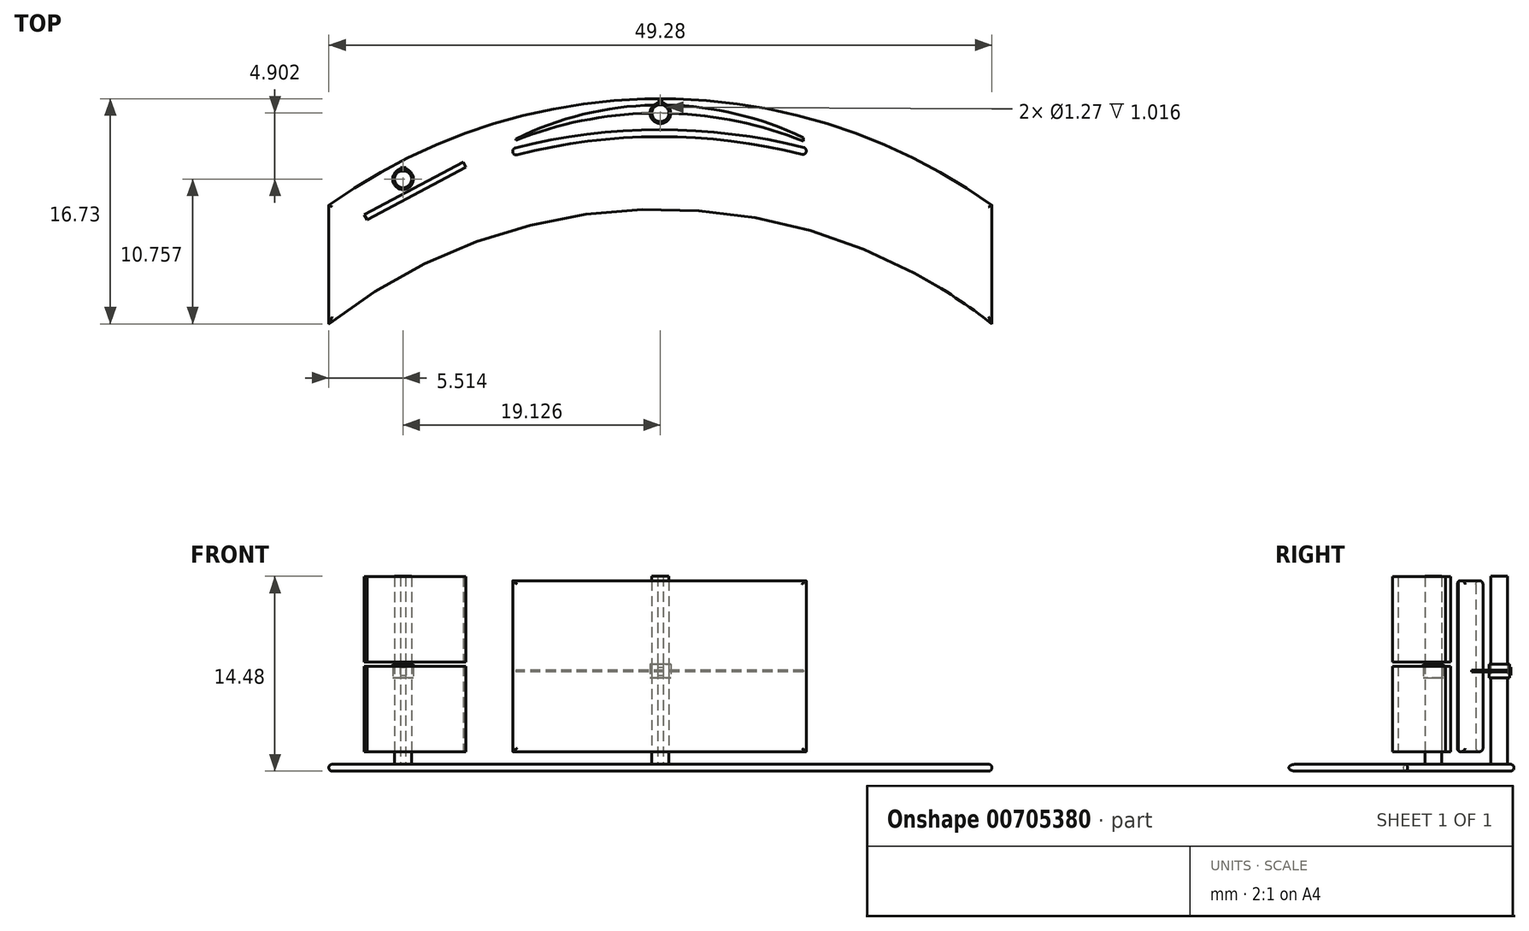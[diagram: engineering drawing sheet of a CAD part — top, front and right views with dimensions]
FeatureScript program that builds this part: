
annotation { "Feature Type Name" : "Feature", "Feature Type Description" : "" }
export const myFeature = defineFeature(function(context is Context, id is Id, definition is map)
    precondition{}
    {
        {
            var Q0;
            Q0=qCreatedBy(makeId("Top.planeOp"),FACE);
            var sketch = newSketch(context, id + "F0", { "sketchPlane" : qUnion([Q0])});
            skArc(sketch, "E0", {"start": v(24.64, 0) * mm, "mid": v(0, 7.91) * mm, "end": v(-24.64, 0) * mm});
            skLineSegment(sketch, "E1", {"start": v(-24.64, 0) * mm, "end": v(-24.64, -8.82) * mm});
            skLineSegment(sketch, "E2", {"start": v(24.64, -8.82) * mm, "end": v(24.64, 0) * mm});
            skArc(sketch, "E3", {"start": v(24.64, -8.82) * mm, "mid": v(0, -0.3) * mm, "end": v(-24.64, -8.82) * mm});
            skCircle(sketch, "E4", {"center": v(0, 6.84) * mm, "radius": 0.64 * mm});
            skCircle(sketch, "E5", {"center": v(-19.12, 1.94) * mm, "radius": 0.64 * mm});
            skCircle(sketch, "E6", {"center": v(18.32, 1.94) * mm, "radius": 0.64 * mm});
            skArc(sketch, "E7", {"start": v(10.63, 5) * mm, "mid": v(-0.07, 7.44) * mm, "end": v(-10.75, 4.93) * mm});
            skLineSegment(sketch, "E8", {"start": v(-10.75, 4.93) * mm, "end": v(-10.75, 4.83) * mm});
            skLineSegment(sketch, "E9", {"start": v(10.63, 5) * mm, "end": v(10.63, 4.75) * mm});
            skArc(sketch, "E10", {"start": v(10.63, 4.75) * mm, "mid": v(-0.06, 6.84) * mm, "end": v(-10.75, 4.83) * mm});
            skCircle(sketch, "E11", {"center": v(0, 6.84) * mm, "radius": 0.77 * mm});
            skLineSegment(sketch, "E12.bottom", {"start": v(-0.21, 7.58) * mm, "end": v(0.2, 7.58) * mm});
            skLineSegment(sketch, "E12.top", {"start": v(-0.21, 7.7) * mm, "end": v(0.2, 7.7) * mm});
            skLineSegment(sketch, "E12.left", {"start": v(-0.21, 7.58) * mm, "end": v(-0.21, 7.7) * mm});
            skLineSegment(sketch, "E12.right", {"start": v(0.2, 7.58) * mm, "end": v(0.2, 7.7) * mm});
            skArc(sketch, "E13", {"start": v(10.84, 4.24) * mm, "mid": v(-0.07, 5.6) * mm, "end": v(-10.98, 4.2) * mm});
            skArc(sketch, "E14", {"start": v(10.84, 3.7) * mm, "mid": v(-0.07, 5.09) * mm, "end": v(-10.98, 3.65) * mm});
            skLineSegment(sketch, "E15", {"start": v(-14.65, 3.22) * mm, "end": v(-22.01, -0.7) * mm});
            skLineSegment(sketch, "E16", {"start": v(-22.01, -0.7) * mm, "end": v(-21.8, -1.1) * mm});
            skLineSegment(sketch, "E17", {"start": v(-21.8, -1.1) * mm, "end": v(-14.45, 2.82) * mm});
            skLineSegment(sketch, "E18", {"start": v(-14.45, 2.82) * mm, "end": v(-14.65, 3.22) * mm});
            skLineSegment(sketch, "E19", {"start": v(-10.98, 4.2) * mm, "end": v(-10.98, 3.65) * mm});
            skLineSegment(sketch, "E20", {"start": v(10.84, 4.24) * mm, "end": v(10.84, 3.7) * mm});
            skSolve(sketch);
        }
        {
            var Q0;
            Q0=makeQuery(id+"F0.imprint","IMPRINT",FACE,{"disambiguationData":[TD([[makeQuery(id+"F0.imprint","IMPRINT",EDGE,{"derivedFrom":sQuery(id+"F0.wireOp",EDGE,"E15")}),1.0]])]});
            var Q1;
            Q1=makeQuery(id+"F0.imprint","IMPRINT",FACE,{"disambiguationData":[TD([[makeQuery(id+"F0.imprint","IMPRINT",EDGE,{"derivedFrom":sQuery(id+"F0.wireOp",EDGE,"E5")}),1.0]])]});
            var Q2;
            {var subQ4=sQuery(id+"F0.wireOp",EDGE,"E12.top");Q2=makeQuery(id+"F0.imprint","IMPRINT",FACE,{"disambiguationData":[TD([[makeQuery(id+"F0.imprint","IMPRINT",EDGE,{"derivedFrom":subQ4}),-1.0]])]});}
            var Q3;
            {var subQ9=sQuery(id+"F0.wireOp",EDGE,"E12.bottom");Q3=makeQuery(id+"F0.imprint","IMPRINT",FACE,{"disambiguationData":[TD([[makeQuery(id+"F0.imprint","IMPRINT",EDGE,{"derivedFrom":subQ9}),-1.0]])]});}
            var Q4;
            {var subQ0=sQuery(id+"F0.wireOp",EDGE,"E12.bottom");Q4=makeQuery(id+"F0.imprint","IMPRINT",FACE,{"disambiguationData":[TD([[makeQuery(id+"F0.imprint","IMPRINT",EDGE,{"derivedFrom":subQ0}),1.0]])]});}
            var Q5;
            {var subQ0=sQuery(id+"F0.wireOp",EDGE,"E7");var subQ1=sQuery(id+"F0.wireOp",EDGE,"E4");var subQ2=makeQuery(id+"F0.imprint","INTERSECT",VERTEX,{"disambiguationData":[OD(0.0)],"derivedFrom":[subQ1,subQ0]});Q5=makeQuery(id+"F0.imprint","IMPRINT",FACE,{"disambiguationData":[TD([[makeQuery(id+"F0.imprint","IMPRINT",EDGE,{"disambiguationData":[TD([[subQ2,1.0]])],"derivedFrom":subQ1}),1.0]])]});}
            var Q6;
            {var subQ0=sQuery(id+"F0.wireOp",EDGE,"E7");var subQ1=sQuery(id+"F0.wireOp",EDGE,"E4");var subQ2=makeQuery(id+"F0.imprint","INTERSECT",VERTEX,{"disambiguationData":[OD(0.0)],"derivedFrom":[subQ1,subQ0]});Q6=makeQuery(id+"F0.imprint","IMPRINT",FACE,{"disambiguationData":[TD([[makeQuery(id+"F0.imprint","IMPRINT",EDGE,{"disambiguationData":[TD([[subQ2,-1.0]])],"derivedFrom":subQ1}),1.0]])]});}
            var Q7;
            {var subQ0=sQuery(id+"F0.wireOp",EDGE,"E7");var subQ1=sQuery(id+"F0.wireOp",EDGE,"E4");var subQ2=makeQuery(id+"F0.imprint","INTERSECT",VERTEX,{"disambiguationData":[OD(0.0)],"derivedFrom":[subQ1,subQ0]});Q7=makeQuery(id+"F0.imprint","IMPRINT",FACE,{"disambiguationData":[TD([[makeQuery(id+"F0.imprint","IMPRINT",EDGE,{"disambiguationData":[TD([[subQ2,-1.0]])],"derivedFrom":subQ1}),-1.0]])]});}
            var Q8;
            {var subQ0=sQuery(id+"F0.wireOp",EDGE,"E7");var subQ1=sQuery(id+"F0.wireOp",EDGE,"E4");var subQ2=makeQuery(id+"F0.imprint","INTERSECT",VERTEX,{"disambiguationData":[OD(1.0)],"derivedFrom":[subQ1,subQ0]});Q8=makeQuery(id+"F0.imprint","IMPRINT",FACE,{"disambiguationData":[TD([[makeQuery(id+"F0.imprint","IMPRINT",EDGE,{"disambiguationData":[TD([[subQ2,1.0]])],"derivedFrom":subQ1}),-1.0]])]});}
            var Q9;
            {var subQ0=sQuery(id+"F0.wireOp",EDGE,"E10");var subQ1=sQuery(id+"F0.wireOp",EDGE,"E4");var subQ2=makeQuery(id+"F0.imprint","INTERSECT",VERTEX,{"disambiguationData":[OD(0.0)],"derivedFrom":[subQ1,subQ0]});Q9=makeQuery(id+"F0.imprint","IMPRINT",FACE,{"disambiguationData":[TD([[makeQuery(id+"F0.imprint","IMPRINT",EDGE,{"disambiguationData":[TD([[subQ2,-1.0]])],"derivedFrom":subQ1}),1.0]])]});}
            var Q10;
            {var subQ0=sQuery(id+"F0.wireOp",EDGE,"E10");var subQ1=sQuery(id+"F0.wireOp",EDGE,"E4");var subQ2=makeQuery(id+"F0.imprint","INTERSECT",VERTEX,{"disambiguationData":[OD(0.0)],"derivedFrom":[subQ1,subQ0]});Q10=makeQuery(id+"F0.imprint","IMPRINT",FACE,{"disambiguationData":[TD([[makeQuery(id+"F0.imprint","IMPRINT",EDGE,{"disambiguationData":[TD([[subQ2,-1.0]])],"derivedFrom":subQ1}),-1.0]])]});}
            var Q11;
            {var subQ0=sQuery(id+"F0.wireOp",EDGE,"E8");Q11=makeQuery(id+"F0.imprint","IMPRINT",FACE,{"disambiguationData":[TD([[makeQuery(id+"F0.imprint","IMPRINT",EDGE,{"derivedFrom":subQ0}),1.0]])]});}
            var Q12;
            {var subQ0=sQuery(id+"F0.wireOp",EDGE,"E9");Q12=makeQuery(id+"F0.imprint","IMPRINT",FACE,{"disambiguationData":[TD([[makeQuery(id+"F0.imprint","IMPRINT",EDGE,{"derivedFrom":subQ0}),-1.0]])]});}
            var Q13;
            Q13=makeQuery(id+"F0.imprint","IMPRINT",FACE,{"disambiguationData":[TD([[makeQuery(id+"F0.imprint","IMPRINT",EDGE,{"derivedFrom":sQuery(id+"F0.wireOp",EDGE,"E13")}),1.0]])]});
            var Q14;
            Q14=makeQuery(id+"F0.imprint","IMPRINT",FACE,{"disambiguationData":[TD([[makeQuery(id+"F0.imprint","IMPRINT",EDGE,{"derivedFrom":sQuery(id+"F0.wireOp",EDGE,"E6")}),1.0]])]});
            var Q15;
            Q15=makeQuery(id+"F0.imprint","IMPRINT",FACE,{"disambiguationData":[TD([[makeQuery(id+"F0.imprint","IMPRINT",EDGE,{"derivedFrom":sQuery(id+"F0.wireOp",EDGE,"E0")}),1.0]])]});
            extrude(context, id + "F1", {"entities" : qUnion([Q0, Q1, Q2, Q3, Q4, Q5, Q6, Q7, Q8, Q9, Q10, Q11, Q12, Q13, Q14, Q15]), "oppositeDirection" : true, "depth" : 0.5 * mm, "offsetDistance" : 25.4 * mm});
        }
        {
            var Q0;
            Q0=makeQuery(id+"F1.opExtrude","CAP_FACE",FACE,{"disambiguationData":[OSD([sQuery(id+"F0.wireOp",EDGE,"E0"),sQuery(id+"F0.wireOp",EDGE,"E1"),sQuery(id+"F0.wireOp",EDGE,"E2"),sQuery(id+"F0.wireOp",EDGE,"E3")])],"isStart":true});
            var Q1;
            Q1=makeQuery(id+"F1.opExtrude","CAP_FACE",FACE,{"disambiguationData":[OSD([sQuery(id+"F0.wireOp",EDGE,"E0"),sQuery(id+"F0.wireOp",EDGE,"E1"),sQuery(id+"F0.wireOp",EDGE,"E2"),sQuery(id+"F0.wireOp",EDGE,"E3")])],"isStart":false});
            fillet(context, id + "F2", {"entities" : qUnion([Q0, Q1]), "radius" : 0.25 * mm, "tangentPropagation" : true, "allowEdgeOverflow" : false});
        }
        {
            var Q0;
            Q0=makeQuery(id+"F0.imprint","IMPRINT",FACE,{"disambiguationData":[TD([[makeQuery(id+"F0.imprint","IMPRINT",EDGE,{"derivedFrom":sQuery(id+"F0.wireOp",EDGE,"E13")}),1.0]])]});
            extrude(context, id + "F3", {"entities" : qUnion([Q0]), "depth" : 12.7 * mm, "offsetDistance" : 25.4 * mm});
        }
        {
            var Q0;
            Q0=makeQuery(id+"F3.opExtrude","SWEPT_BODY",BODY,{"disambiguationData":[OSD([sQuery(id+"F0.wireOp",EDGE,"E13"),sQuery(id+"F0.wireOp",EDGE,"E14"),sQuery(id+"F0.wireOp",EDGE,"E19"),sQuery(id+"F0.wireOp",EDGE,"E20")])]});
            transform(context, id + "F4", {"entities" : qUnion([Q0]), "transformType" : TransformType.TRANSLATION_3D, "dx" : 0 * mm, "dy" : 0 * mm, "dz" : 0.94 * mm, "makeCopy" : false});
        }
        {
            var Q0;
            Q0=makeQuery(id+"F0.imprint","IMPRINT",FACE,{"disambiguationData":[TD([[makeQuery(id+"F0.imprint","IMPRINT",EDGE,{"derivedFrom":sQuery(id+"F0.wireOp",EDGE,"E15")}),1.0]])]});
            extrude(context, id + "F5", {"entities" : qUnion([Q0]), "depth" : 6.35 * mm, "offsetDistance" : 25.4 * mm});
        }
        {
            var Q0;
            Q0=makeQuery(id+"F5.opExtrude","SWEPT_BODY",BODY,{"disambiguationData":[OSD([sQuery(id+"F0.wireOp",EDGE,"E15"),sQuery(id+"F0.wireOp",EDGE,"E16"),sQuery(id+"F0.wireOp",EDGE,"E17"),sQuery(id+"F0.wireOp",EDGE,"E18")])]});
            transform(context, id + "F6", {"entities" : qUnion([Q0]), "transformType" : TransformType.TRANSLATION_3D, "dx" : 0 * mm, "dy" : 0 * mm, "dz" : 0.94 * mm, "makeCopy" : false});
        }
        {
            var Q0;
            Q0=makeQuery(id+"F5.opExtrude","SWEPT_BODY",BODY,{"disambiguationData":[OSD([sQuery(id+"F0.wireOp",EDGE,"E15"),sQuery(id+"F0.wireOp",EDGE,"E16"),sQuery(id+"F0.wireOp",EDGE,"E17"),sQuery(id+"F0.wireOp",EDGE,"E18")])]});
            transform(context, id + "F7", {"entities" : qUnion([Q0]), "transformType" : TransformType.TRANSLATION_3D, "dx" : 0 * mm, "dy" : 0 * mm, "dz" : 6.65 * mm, "makeCopy" : true});
        }
        {
            var Q0;
            {var subQ0=sQuery(id+"F0.wireOp",EDGE,"E10");var subQ1=sQuery(id+"F0.wireOp",EDGE,"E4");var subQ2=makeQuery(id+"F0.imprint","INTERSECT",VERTEX,{"disambiguationData":[OD(0.0)],"derivedFrom":[subQ1,subQ0]});Q0=makeQuery(id+"F0.imprint","IMPRINT",FACE,{"disambiguationData":[TD([[makeQuery(id+"F0.imprint","IMPRINT",EDGE,{"disambiguationData":[TD([[subQ2,-1.0]])],"derivedFrom":subQ1}),1.0]])]});}
            var Q1;
            {var subQ0=sQuery(id+"F0.wireOp",EDGE,"E7");var subQ1=sQuery(id+"F0.wireOp",EDGE,"E4");var subQ2=makeQuery(id+"F0.imprint","INTERSECT",VERTEX,{"disambiguationData":[OD(0.0)],"derivedFrom":[subQ1,subQ0]});Q1=makeQuery(id+"F0.imprint","IMPRINT",FACE,{"disambiguationData":[TD([[makeQuery(id+"F0.imprint","IMPRINT",EDGE,{"disambiguationData":[TD([[subQ2,-1.0]])],"derivedFrom":subQ1}),1.0]])]});}
            extrude(context, id + "F8", {"entities" : qUnion([Q0, Q1]), "depth" : 13.97 * mm, "offsetDistance" : 25.4 * mm});
        }
        {
            var Q0;
            {var subQ0=sQuery(id+"F0.wireOp",EDGE,"E10");var subQ1=sQuery(id+"F0.wireOp",EDGE,"E4");var subQ2=makeQuery(id+"F0.imprint","INTERSECT",VERTEX,{"disambiguationData":[OD(0.0)],"derivedFrom":[subQ1,subQ0]});Q0=makeQuery(id+"F0.imprint","IMPRINT",FACE,{"disambiguationData":[TD([[makeQuery(id+"F0.imprint","IMPRINT",EDGE,{"disambiguationData":[TD([[subQ2,-1.0]])],"derivedFrom":subQ1}),-1.0]])]});}
            var Q1;
            {var subQ0=sQuery(id+"F0.wireOp",EDGE,"E7");var subQ1=sQuery(id+"F0.wireOp",EDGE,"E4");var subQ2=makeQuery(id+"F0.imprint","INTERSECT",VERTEX,{"disambiguationData":[OD(0.0)],"derivedFrom":[subQ1,subQ0]});Q1=makeQuery(id+"F0.imprint","IMPRINT",FACE,{"disambiguationData":[TD([[makeQuery(id+"F0.imprint","IMPRINT",EDGE,{"disambiguationData":[TD([[subQ2,-1.0]])],"derivedFrom":subQ1}),-1.0]])]});}
            var Q2;
            {var subQ0=sQuery(id+"F0.wireOp",EDGE,"E7");var subQ1=sQuery(id+"F0.wireOp",EDGE,"E4");var subQ2=makeQuery(id+"F0.imprint","INTERSECT",VERTEX,{"disambiguationData":[OD(1.0)],"derivedFrom":[subQ1,subQ0]});Q2=makeQuery(id+"F0.imprint","IMPRINT",FACE,{"disambiguationData":[TD([[makeQuery(id+"F0.imprint","IMPRINT",EDGE,{"disambiguationData":[TD([[subQ2,1.0]])],"derivedFrom":subQ1}),-1.0]])]});}
            var Q3;
            {var subQ9=sQuery(id+"F0.wireOp",EDGE,"E12.bottom");Q3=makeQuery(id+"F0.imprint","IMPRINT",FACE,{"disambiguationData":[TD([[makeQuery(id+"F0.imprint","IMPRINT",EDGE,{"derivedFrom":subQ9}),-1.0]])]});}
            extrude(context, id + "F9", {"entities" : qUnion([Q0, Q1, Q2, Q3]), "depth" : 1.02 * mm, "offsetDistance" : 25.4 * mm});
        }
        {
            var Q0;
            {var subQ4=sQuery(id+"F0.wireOp",EDGE,"E12.top");Q0=makeQuery(id+"F0.imprint","IMPRINT",FACE,{"disambiguationData":[TD([[makeQuery(id+"F0.imprint","IMPRINT",EDGE,{"derivedFrom":subQ4}),-1.0]])]});}
            var Q1;
            {var subQ0=sQuery(id+"F0.wireOp",EDGE,"E12.bottom");Q1=makeQuery(id+"F0.imprint","IMPRINT",FACE,{"disambiguationData":[TD([[makeQuery(id+"F0.imprint","IMPRINT",EDGE,{"derivedFrom":subQ0}),1.0]])]});}
            extrude(context, id + "F10", {"entities" : qUnion([Q0, Q1]), "depth" : 0.6 * mm, "offsetDistance" : 25.4 * mm});
        }
        {
            var Q0;
            Q0=makeQuery(id+"F10.opExtrude","SWEPT_BODY",BODY,{"disambiguationData":[OSD([sQuery(id+"F0.wireOp",EDGE,"E12.bottom"),sQuery(id+"F0.wireOp",EDGE,"E12.top"),sQuery(id+"F0.wireOp",EDGE,"E12.left"),sQuery(id+"F0.wireOp",EDGE,"E12.right")])]});
            transform(context, id + "F11", {"entities" : qUnion([Q0]), "transformType" : TransformType.TRANSLATION_3D, "dx" : 0 * mm, "dy" : 0 * mm, "dz" : 0.19 * mm, "makeCopy" : false});
        }
        {
            var Q0;
            Q0=makeQuery(id+"F10.opExtrude","SWEPT_BODY",BODY,{"disambiguationData":[OSD([sQuery(id+"F0.wireOp",EDGE,"E12.bottom"),sQuery(id+"F0.wireOp",EDGE,"E12.top"),sQuery(id+"F0.wireOp",EDGE,"E12.left"),sQuery(id+"F0.wireOp",EDGE,"E12.right")])]});
            var Q1;
            Q1=makeQuery(id+"F9.opExtrude","SWEPT_BODY",BODY,{"disambiguationData":[OSD([sQuery(id+"F0.wireOp",EDGE,"E4"),sQuery(id+"F0.wireOp",EDGE,"E11"),sQuery(id+"F0.wireOp",EDGE,"E12.bottom"),sQuery(id+"F0.wireOp",EDGE,"E12.right")])]});
            transform(context, id + "F12", {"entities" : qUnion([Q0, Q1]), "transformType" : TransformType.TRANSLATION_3D, "dx" : 0 * mm, "dy" : 0 * mm, "dz" : 6.43 * mm, "makeCopy" : false});
        }
        {
            var Q0;
            Q0=makeQuery(id+"F8.opExtrude","SWEPT_BODY",BODY,{"disambiguationData":[OSD([sQuery(id+"F0.wireOp",EDGE,"E4"),sQuery(id+"F0.wireOp",EDGE,"E7")])]});
            transform(context, id + "F13", {"entities" : qUnion([Q0]), "transformType" : TransformType.TRANSLATION_3D, "dx" : -19.13 * mm, "dy" : -4.9 * mm, "dz" : 0 * mm, "makeCopy" : true});
        }
        {
            var Q0;
            Q0=makeQuery(id+"F9.opExtrude","SWEPT_BODY",BODY,{"disambiguationData":[OSD([sQuery(id+"F0.wireOp",EDGE,"E4"),sQuery(id+"F0.wireOp",EDGE,"E11"),sQuery(id+"F0.wireOp",EDGE,"E12.bottom"),sQuery(id+"F0.wireOp",EDGE,"E12.right")])]});
            transform(context, id + "F14", {"entities" : qUnion([Q0]), "transformType" : TransformType.TRANSLATION_3D, "dx" : -19.13 * mm, "dy" : -4.9 * mm, "dz" : 0 * mm, "makeCopy" : true});
        }
        {
            var Q0;
            Q0=makeQuery(id+"F10.opExtrude","SWEPT_BODY",BODY,{"disambiguationData":[OSD([sQuery(id+"F0.wireOp",EDGE,"E12.bottom"),sQuery(id+"F0.wireOp",EDGE,"E12.top"),sQuery(id+"F0.wireOp",EDGE,"E12.left"),sQuery(id+"F0.wireOp",EDGE,"E12.right")])]});
            transform(context, id + "F15", {"entities" : qUnion([Q0]), "transformType" : TransformType.TRANSLATION_3D, "dx" : -19.12 * mm, "dy" : -4.9 * mm, "dz" : 0 * mm, "makeCopy" : true});
        }
        {
            var Q0;
            Q0=makeQuery(id+"F3.opExtrude","SWEPT_FACE",FACE,{"disambiguationData":[OSD([sQuery(id+"F0.wireOp",EDGE,"E14")])]});
            fillet(context, id + "F16", {"entities" : qUnion([Q0]), "radius" : 0.25 * mm, "tangentPropagation" : true, "allowEdgeOverflow" : false});
        }
        {
            var Q0;
            Q0=makeQuery(id+"F3.opExtrude","SWEPT_BODY",BODY,{"disambiguationData":[OSD([sQuery(id+"F0.wireOp",EDGE,"E13"),sQuery(id+"F0.wireOp",EDGE,"E14"),sQuery(id+"F0.wireOp",EDGE,"E19"),sQuery(id+"F0.wireOp",EDGE,"E20")])]});
            transform(context, id + "F17", {"entities" : qUnion([Q0]), "transformType" : TransformType.TRANSLATION_3D, "dx" : 0 * mm, "dy" : 0 * mm, "dz" : 0 * mm, "makeCopy" : true});
        }
        {
            var Q0;
            Q0=makeQuery(id+"F17.opPattern","COPY",BODY,{"derivedFrom":makeQuery(id+"F3.opExtrude","SWEPT_BODY",BODY,{"disambiguationData":[OSD([sQuery(id+"F0.wireOp",EDGE,"E13"),sQuery(id+"F0.wireOp",EDGE,"E14"),sQuery(id+"F0.wireOp",EDGE,"E19"),sQuery(id+"F0.wireOp",EDGE,"E20")])]}),"instanceName":"1"});
            deleteBodies(context, id + "F18", {"entities" : qUnion([Q0])});
        }
        {
            var Q0;
            Q0=makeQuery(id+"F3.opExtrude","SWEPT_FACE",FACE,{"disambiguationData":[OSD([sQuery(id+"F0.wireOp",EDGE,"E13")])]});
            fillet(context, id + "F19", {"entities" : qUnion([Q0]), "radius" : 0.25 * mm, "tangentPropagation" : true, "allowEdgeOverflow" : false});
        }
        {
            var Q0;
            {var subQ0=sQuery(id+"F0.wireOp",EDGE,"E9");Q0=makeQuery(id+"F0.imprint","IMPRINT",FACE,{"disambiguationData":[TD([[makeQuery(id+"F0.imprint","IMPRINT",EDGE,{"derivedFrom":subQ0}),-1.0]])]});}
            var Q1;
            {var subQ0=sQuery(id+"F0.wireOp",EDGE,"E8");Q1=makeQuery(id+"F0.imprint","IMPRINT",FACE,{"disambiguationData":[TD([[makeQuery(id+"F0.imprint","IMPRINT",EDGE,{"derivedFrom":subQ0}),1.0]])]});}
            var Q2;
            {var subQ0=sQuery(id+"F0.wireOp",EDGE,"E7");var subQ1=sQuery(id+"F0.wireOp",EDGE,"E4");var subQ2=makeQuery(id+"F0.imprint","INTERSECT",VERTEX,{"disambiguationData":[OD(0.0)],"derivedFrom":[subQ1,subQ0]});Q2=makeQuery(id+"F0.imprint","IMPRINT",FACE,{"disambiguationData":[TD([[makeQuery(id+"F0.imprint","IMPRINT",EDGE,{"disambiguationData":[TD([[subQ2,-1.0]])],"derivedFrom":subQ1}),1.0]])]});}
            var Q3;
            {var subQ0=sQuery(id+"F0.wireOp",EDGE,"E7");var subQ1=sQuery(id+"F0.wireOp",EDGE,"E4");var subQ2=makeQuery(id+"F0.imprint","INTERSECT",VERTEX,{"disambiguationData":[OD(1.0)],"derivedFrom":[subQ1,subQ0]});Q3=makeQuery(id+"F0.imprint","IMPRINT",FACE,{"disambiguationData":[TD([[makeQuery(id+"F0.imprint","IMPRINT",EDGE,{"disambiguationData":[TD([[subQ2,1.0]])],"derivedFrom":subQ1}),-1.0]])]});}
            var Q4;
            {var subQ0=sQuery(id+"F0.wireOp",EDGE,"E7");var subQ1=sQuery(id+"F0.wireOp",EDGE,"E4");var subQ2=makeQuery(id+"F0.imprint","INTERSECT",VERTEX,{"disambiguationData":[OD(0.0)],"derivedFrom":[subQ1,subQ0]});Q4=makeQuery(id+"F0.imprint","IMPRINT",FACE,{"disambiguationData":[TD([[makeQuery(id+"F0.imprint","IMPRINT",EDGE,{"disambiguationData":[TD([[subQ2,-1.0]])],"derivedFrom":subQ1}),-1.0]])]});}
            extrude(context, id + "F20", {"entities" : qUnion([Q0, Q1, Q2, Q3, Q4]), "depth" : 0.13 * mm, "offsetDistance" : 25.4 * mm});
        }
        {
            var Q0;
            Q0=makeQuery(id+"F20.opExtrude","SWEPT_BODY",BODY,{"disambiguationData":[OSD([sQuery(id+"F0.wireOp",EDGE,"E7"),sQuery(id+"F0.wireOp",EDGE,"E8"),sQuery(id+"F0.wireOp",EDGE,"E9"),sQuery(id+"F0.wireOp",EDGE,"E10")])]});
            transform(context, id + "F21", {"entities" : qUnion([Q0]), "transformType" : TransformType.TRANSLATION_3D, "dx" : 0 * mm, "dy" : 0 * mm, "dz" : 6.86 * mm, "makeCopy" : false});
        }
    });
